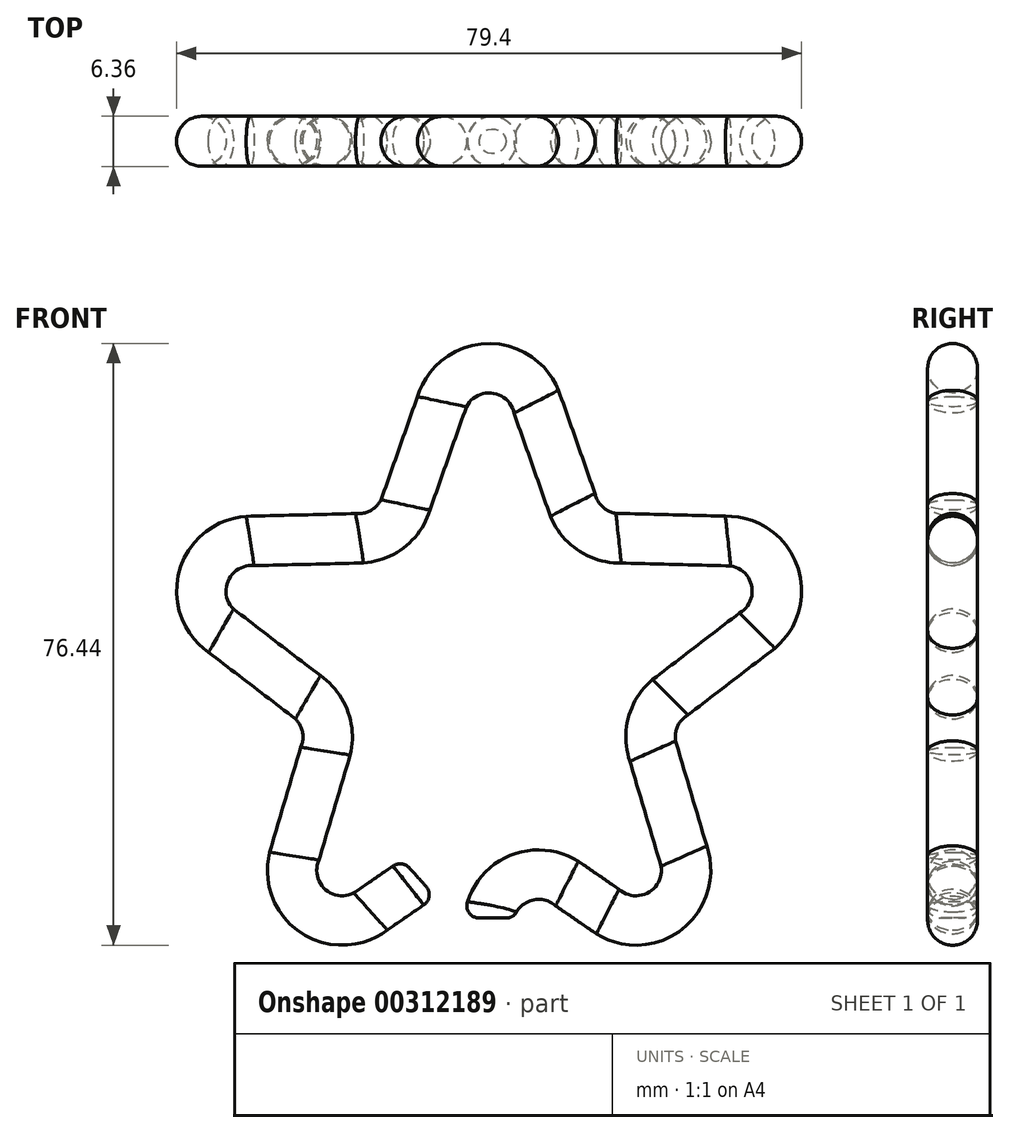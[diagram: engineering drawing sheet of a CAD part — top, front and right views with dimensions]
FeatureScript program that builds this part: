
annotation { "Feature Type Name" : "Feature", "Feature Type Description" : "" }
export const myFeature = defineFeature(function(context is Context, id is Id, definition is map)
    precondition{}
    {
        {
            var Q0;
            Q0=qCreatedBy(makeId("Front.planeOp"),FACE);
            var sketch = newSketch(context, id + "F0", { "sketchPlane" : qUnion([Q0])});
            skCircle(sketch, "E0.cCircle", {"center": v(0, 31.75) * mm, "radius": 25.4 * mm, "construction": true});
            skLineSegment(sketch, "E0.0", {"start": v(14.93, 11.2) * mm, "end": v(-14.93, 11.2) * mm, "construction": true});
            skLineSegment(sketch, "E0.1", {"start": v(-14.93, 11.2) * mm, "end": v(-24.16, 39.6) * mm, "construction": true});
            skLineSegment(sketch, "E0.2", {"start": v(-24.16, 39.6) * mm, "end": v(0, 57.15) * mm, "construction": true});
            skLineSegment(sketch, "E0.3", {"start": v(0, 57.15) * mm, "end": v(24.16, 39.6) * mm, "construction": true});
            skLineSegment(sketch, "E0.4", {"start": v(24.16, 39.6) * mm, "end": v(14.93, 11.2) * mm, "construction": true});
            skLineSegment(sketch, "E1", {"start": v(0, 31.75) * mm, "end": v(-48.31, 47.45) * mm, "construction": true});
            skLineSegment(sketch, "E2", {"start": v(0, 31.75) * mm, "end": v(0, 82.55) * mm, "construction": true});
            skLineSegment(sketch, "E3", {"start": v(0, 31.75) * mm, "end": v(48.31, 47.45) * mm, "construction": true});
            skLineSegment(sketch, "E4", {"start": v(0, 31.75) * mm, "end": v(29.86, -9.35) * mm, "construction": true});
            skLineSegment(sketch, "E5", {"start": v(0, 31.75) * mm, "end": v(-29.86, -9.35) * mm, "construction": true});
            skLineSegment(sketch, "E6", {"start": v(9.9, 4.4) * mm, "end": v(15.06, 0.84) * mm});
            skLineSegment(sketch, "E7", {"start": v(20.79, 21.21) * mm, "end": v(24.75, 7.88) * mm});
            skLineSegment(sketch, "E8", {"start": v(23.01, 28.06) * mm, "end": v(34.05, 36.52) * mm});
            skLineSegment(sketch, "E9", {"start": v(30.35, 47.9) * mm, "end": v(16.45, 48.26) * mm});
            skLineSegment(sketch, "E10", {"start": v(10.62, 52.5) * mm, "end": v(5.99, 65.6) * mm});
            skLineSegment(sketch, "E11", {"start": v(-10.62, 52.5) * mm, "end": v(-5.99, 65.6) * mm});
            skLineSegment(sketch, "E12", {"start": v(-16.45, 48.26) * mm, "end": v(-30.35, 47.9) * mm});
            skLineSegment(sketch, "E13", {"start": v(-20.79, 21.21) * mm, "end": v(-24.75, 7.88) * mm});
            skLineSegment(sketch, "E14", {"start": v(-34.05, 36.52) * mm, "end": v(-23.01, 28.06) * mm});
            skLineSegment(sketch, "E15", {"start": v(-15.06, 0.84) * mm, "end": v(-8.94, 5.05) * mm});
            skLineSegment(sketch, "E16", {"start": v(0, 11.2) * mm, "end": v(-15.06, 0.84) * mm, "construction": true});
            skArc(sketch, "E17", {"start": v(-30.35, 47.9) * mm, "mid": v(-36.23, 43.52) * mm, "end": v(-34.05, 36.52) * mm});
            skArc(sketch, "E18", {"start": v(5.99, 65.6) * mm, "mid": v(0, 69.84) * mm, "end": v(-5.99, 65.6) * mm});
            skArc(sketch, "E19", {"start": v(34.05, 36.52) * mm, "mid": v(36.23, 43.52) * mm, "end": v(30.35, 47.9) * mm});
            skArc(sketch, "E20", {"start": v(15.06, 0.84) * mm, "mid": v(22.4, 0.93) * mm, "end": v(24.75, 7.88) * mm});
            skArc(sketch, "E21", {"start": v(-24.75, 7.88) * mm, "mid": v(-22.4, 0.93) * mm, "end": v(-15.06, 0.84) * mm});
            skArc(sketch, "E22", {"start": v(9.9, 4.4) * mm, "mid": v(3.72, 4.96) * mm, "end": v(0, 0) * mm});
            skArc(sketch, "E23", {"start": v(-16.45, 48.26) * mm, "mid": v(-12.88, 49.47) * mm, "end": v(-10.62, 52.5) * mm});
            skArc(sketch, "E24", {"start": v(-20.79, 21.21) * mm, "mid": v(-20.84, 24.98) * mm, "end": v(-23.01, 28.06) * mm});
            skArc(sketch, "E25", {"start": v(23.01, 28.06) * mm, "mid": v(20.84, 24.98) * mm, "end": v(20.79, 21.21) * mm});
            skArc(sketch, "E26", {"start": v(10.62, 52.5) * mm, "mid": v(12.88, 49.47) * mm, "end": v(16.45, 48.26) * mm});
            skPoint(sketch, "E27.orphan", {"position": v(-12.08, 48.37) * mm});
            skPoint(sketch, "E28.orphan", {"position": v(12.08, 48.37) * mm});
            skPoint(sketch, "E29.orphan", {"position": v(19.54, 25.4) * mm});
            skPoint(sketch, "E30.orphan", {"position": v(-19.54, 25.4) * mm});
            skSolve(sketch);
        }
        {
            var Q0;
            Q0=qCreatedBy(makeId("Top.planeOp"),FACE);
            var sketch = newSketch(context, id + "F1", { "sketchPlane" : qUnion([Q0])});
            skCircle(sketch, "E31", {"center": v(0, 0) * mm, "radius": 3.18 * mm});
            skSolve(sketch);
        }
        {
            var Q0;
            Q0=makeQuery(id+"F1.imprint","IMPRINT",FACE,{"disambiguationData":[TD([[makeQuery(id+"F1.imprint","IMPRINT",EDGE,{"derivedFrom":sQuery(id+"F1.wireOp",EDGE,"E31")}),1.0]])]});
            var Q1;
            Q1 = qConstructionFilter(qBodyType(qCreatedBy(id + "F0" ,EDGE), BodyType.WIRE), ConstructionObject.NO);
            sweep(context, id + "F2", {"profiles" : qUnion([Q0]), "path" : qUnion([Q1])});
        }
        {
            var Q0;
            Q0=makeQuery(id+"F2.opSweep","CAP_EDGE",EDGE,{"disambiguationData":[OSD([sQuery(id+"F0.wireOp",VERTEX,"E15.end"),sQuery(id+"F1.wireOp",EDGE,"E31")])],"isStart":false});
            var Q1;
            Q1=makeQuery(id+"F2.opSweep","CAP_EDGE",EDGE,{"disambiguationData":[OSD([sQuery(id+"F0.wireOp",VERTEX,"E22.end"),sQuery(id+"F1.wireOp",EDGE,"E31")])],"isStart":true});
            fillet(context, id + "F3", {"entities" : qUnion([Q0, Q1]), "radius" : 1.59 * mm, "tangentPropagation" : true, "allowEdgeOverflow" : false});
        }
    });
